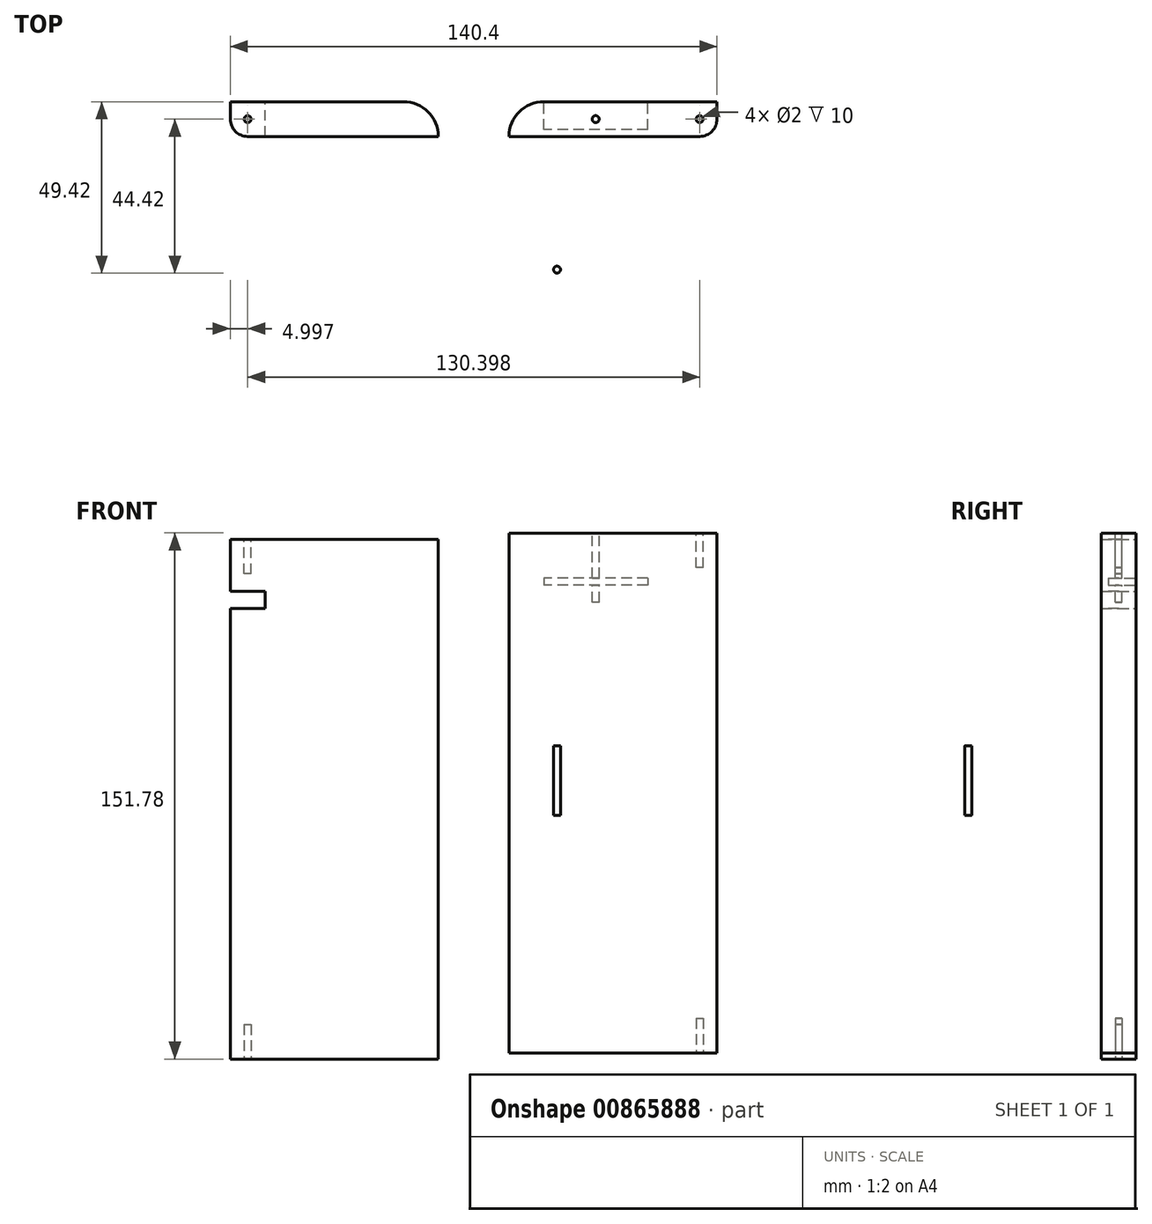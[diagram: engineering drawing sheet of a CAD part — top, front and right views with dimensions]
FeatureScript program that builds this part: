
annotation { "Feature Type Name" : "Feature", "Feature Type Description" : "" }
export const myFeature = defineFeature(function(context is Context, id is Id, definition is map)
    precondition{}
    {
        {
            var Q0;
            Q0=qCreatedBy(makeId("Front.planeOp"),FACE);
            var sketch = newSketch(context, id + "F0", { "sketchPlane" : qUnion([Q0])});
            skLineSegment(sketch, "E0.bottom", {"start": v(-77.65, 79.68) * mm, "end": v(-17.65, 79.68) * mm});
            skLineSegment(sketch, "E0.top", {"start": v(-77.65, -70.32) * mm, "end": v(-17.65, -70.32) * mm});
            skLineSegment(sketch, "E0.left", {"start": v(-77.65, 79.68) * mm, "end": v(-77.65, 64.68) * mm});
            skLineSegment(sketch, "E0.right", {"start": v(-17.65, 79.68) * mm, "end": v(-17.65, -70.32) * mm});
            skLineSegment(sketch, "E1.bottom", {"start": v(-77.65, 64.68) * mm, "end": v(-67.65, 64.68) * mm});
            skLineSegment(sketch, "E1.top", {"start": v(-77.65, 59.68) * mm, "end": v(-67.65, 59.68) * mm});
            skLineSegment(sketch, "E1.right", {"start": v(-67.65, 64.68) * mm, "end": v(-67.65, 59.68) * mm});
            skLineSegment(sketch, "E2.trimOffspring", {"start": v(-77.65, 59.68) * mm, "end": v(-77.65, -70.32) * mm});
            skLineSegment(sketch, "E3.bottom", {"start": v(2.75, 81.46) * mm, "end": v(62.75, 81.46) * mm});
            skLineSegment(sketch, "E3.top", {"start": v(2.75, -68.54) * mm, "end": v(62.75, -68.54) * mm});
            skLineSegment(sketch, "E3.left", {"start": v(2.75, 81.46) * mm, "end": v(2.75, -68.54) * mm});
            skLineSegment(sketch, "E3.right", {"start": v(62.75, 81.46) * mm, "end": v(62.75, -68.54) * mm});
            skSolve(sketch);
        }
        {
            var Q0;
            Q0=qSketchRegion(id+"F0",true);
            extrude(context, id + "F1", {"entities" : qUnion([Q0]), "depth" : 10 * mm, "offsetDistance" : 25 * mm});
        }
        {
            var Q0;
            Q0=makeQuery(id+"F1.opExtrude","CAP_EDGE",EDGE,{"disambiguationData":[OSD([sQuery(id+"F0.wireOp",EDGE,"E0.left")])],"isStart":false});
            var Q1;
            Q1=makeQuery(id+"F1.opExtrude","CAP_EDGE",EDGE,{"disambiguationData":[OSD([sQuery(id+"F0.wireOp",EDGE,"E2.trimOffspring")])],"isStart":false});
            var Q2;
            Q2=makeQuery(id+"F1.opExtrude","CAP_EDGE",EDGE,{"disambiguationData":[OSD([sQuery(id+"F0.wireOp",EDGE,"E3.right")])],"isStart":false});
            fillet(context, id + "F2", {"entities" : qUnion([Q0, Q1, Q2]), "radius" : 5 * mm, "tangentPropagation" : true, "allowEdgeOverflow" : false});
        }
        {
            var Q0;
            Q0=makeQuery(id+"F1.opExtrude","CAP_FACE",FACE,{"disambiguationData":[OSD([sQuery(id+"F0.wireOp",EDGE,"E3.bottom"),sQuery(id+"F0.wireOp",EDGE,"E3.top"),sQuery(id+"F0.wireOp",EDGE,"E3.left"),sQuery(id+"F0.wireOp",EDGE,"E3.right")])],"isStart":true});
            var sketch = newSketch(context, id + "F3", { "sketchPlane" : qUnion([Q0])});
            skLineSegment(sketch, "E4.bottom", {"start": v(-42.75, 68.46) * mm, "end": v(-12.75, 68.46) * mm});
            skLineSegment(sketch, "E4.top", {"start": v(-42.75, 66.46) * mm, "end": v(-12.75, 66.46) * mm});
            skLineSegment(sketch, "E4.left", {"start": v(-42.75, 68.46) * mm, "end": v(-42.75, 66.46) * mm});
            skLineSegment(sketch, "E4.right", {"start": v(-12.75, 68.46) * mm, "end": v(-12.75, 66.46) * mm});
            skSolve(sketch);
        }
        {
            var Q0;
            Q0=makeQuery(id+"F1.opExtrude","CAP_EDGE",EDGE,{"disambiguationData":[OSD([sQuery(id+"F0.wireOp",EDGE,"E3.left")])],"isStart":true});
            var Q1;
            Q1=makeQuery(id+"F1.opExtrude","CAP_EDGE",EDGE,{"disambiguationData":[OSD([sQuery(id+"F0.wireOp",EDGE,"E0.right")])],"isStart":true});
            fillet(context, id + "F4", {"entities" : qUnion([Q0, Q1]), "radius" : 10 * mm, "tangentPropagation" : true, "allowEdgeOverflow" : false});
        }
        {
            var Q0;
            Q0=qSketchRegion(id+"F3",true);
            extrude(context, id + "F5", {"entities" : qUnion([Q0]), "operationType" : NewBodyOperationType.REMOVE, "oppositeDirection" : true, "depth" : 8 * mm, "offsetDistance" : 25 * mm});
        }
        {
            var Q0;
            Q0=makeQuery(id+"F1.opExtrude","SWEPT_FACE",FACE,{"disambiguationData":[OSD([sQuery(id+"F0.wireOp",EDGE,"E3.bottom")])]});
            var sketch = newSketch(context, id + "F6", { "sketchPlane" : qUnion([Q0])});
            skCircle(sketch, "E5", {"center": v(27.75, -5) * mm, "radius": 1 * mm});
            skSolve(sketch);
        }
        {
            var Q0;
            Q0=qSketchRegion(id+"F6",true);
            extrude(context, id + "F7", {"entities" : qUnion([Q0]), "operationType" : NewBodyOperationType.REMOVE, "oppositeDirection" : true, "depth" : 20 * mm, "offsetDistance" : 25 * mm});
        }
        {
            var Q0;
            Q0=makeQuery(id+"F1.opExtrude","SWEPT_FACE",FACE,{"disambiguationData":[OSD([sQuery(id+"F0.wireOp",EDGE,"E0.top")])]});
            var sketch = newSketch(context, id + "F8", { "sketchPlane" : qUnion([Q0])});
            skCircle(sketch, "E6", {"center": v(-72.65, 5) * mm, "radius": 1 * mm});
            skSolve(sketch);
        }
        {
            var Q0;
            Q0=qSketchRegion(id+"F8",true);
            extrude(context, id + "F9", {"entities" : qUnion([Q0]), "operationType" : NewBodyOperationType.REMOVE, "oppositeDirection" : true, "depth" : 10 * mm, "offsetDistance" : 25 * mm});
        }
        {
            var Q0;
            Q0=makeQuery(id+"F1.opExtrude","SWEPT_FACE",FACE,{"disambiguationData":[OSD([sQuery(id+"F0.wireOp",EDGE,"E3.top")])]});
            var sketch = newSketch(context, id + "F10", { "sketchPlane" : qUnion([Q0])});
            skCircle(sketch, "E7", {"center": v(57.75, 5) * mm, "radius": 1 * mm});
            skSolve(sketch);
        }
        {
            var Q0;
            Q0=qSketchRegion(id+"F10",true);
            extrude(context, id + "F11", {"entities" : qUnion([Q0]), "operationType" : NewBodyOperationType.REMOVE, "oppositeDirection" : true, "depth" : 10 * mm, "offsetDistance" : 25 * mm});
        }
        {
            var Q0;
            Q0=makeQuery(id+"F1.opExtrude","SWEPT_FACE",FACE,{"disambiguationData":[OSD([sQuery(id+"F0.wireOp",EDGE,"E0.bottom")])]});
            var sketch = newSketch(context, id + "F12", { "sketchPlane" : qUnion([Q0])});
            skCircle(sketch, "E8", {"center": v(-72.65, -5) * mm, "radius": 1 * mm});
            skSolve(sketch);
        }
        {
            var Q0;
            Q0=qSketchRegion(id+"F12",true);
            extrude(context, id + "F13", {"entities" : qUnion([Q0]), "operationType" : NewBodyOperationType.REMOVE, "oppositeDirection" : true, "depth" : 10 * mm, "offsetDistance" : 25 * mm});
        }
        {
            var Q0;
            Q0=makeQuery(id+"F1.opExtrude","SWEPT_FACE",FACE,{"disambiguationData":[OSD([sQuery(id+"F0.wireOp",EDGE,"E3.bottom")])]});
            var sketch = newSketch(context, id + "F14", { "sketchPlane" : qUnion([Q0])});
            skCircle(sketch, "E9", {"center": v(57.75, -5) * mm, "radius": 1 * mm});
            skSolve(sketch);
        }
        {
            var Q0;
            Q0 = qSketchRegion(id + "F14", true);
            extrude(context, id + "F15", {"entities" : qUnion([Q0]), "operationType" : NewBodyOperationType.REMOVE, "oppositeDirection" : true, "depth" : 10 * mm, "offsetDistance" : 25 * mm});
        }
        {
            var Q0;
            Q0=qCreatedBy(makeId("Top.planeOp"),FACE);
            var sketch = newSketch(context, id + "F16", { "sketchPlane" : qUnion([Q0])});
            skCircle(sketch, "E10", {"center": v(16.58, -48.42) * mm, "radius": 1 * mm});
            skSolve(sketch);
        }
        {
            var Q0;
            Q0 = qSketchRegion(id + "F16", true);
            extrude(context, id + "F17", {"entities" : qUnion([Q0]), "depth" : 20 * mm, "offsetDistance" : 25 * mm});
        }
    });
